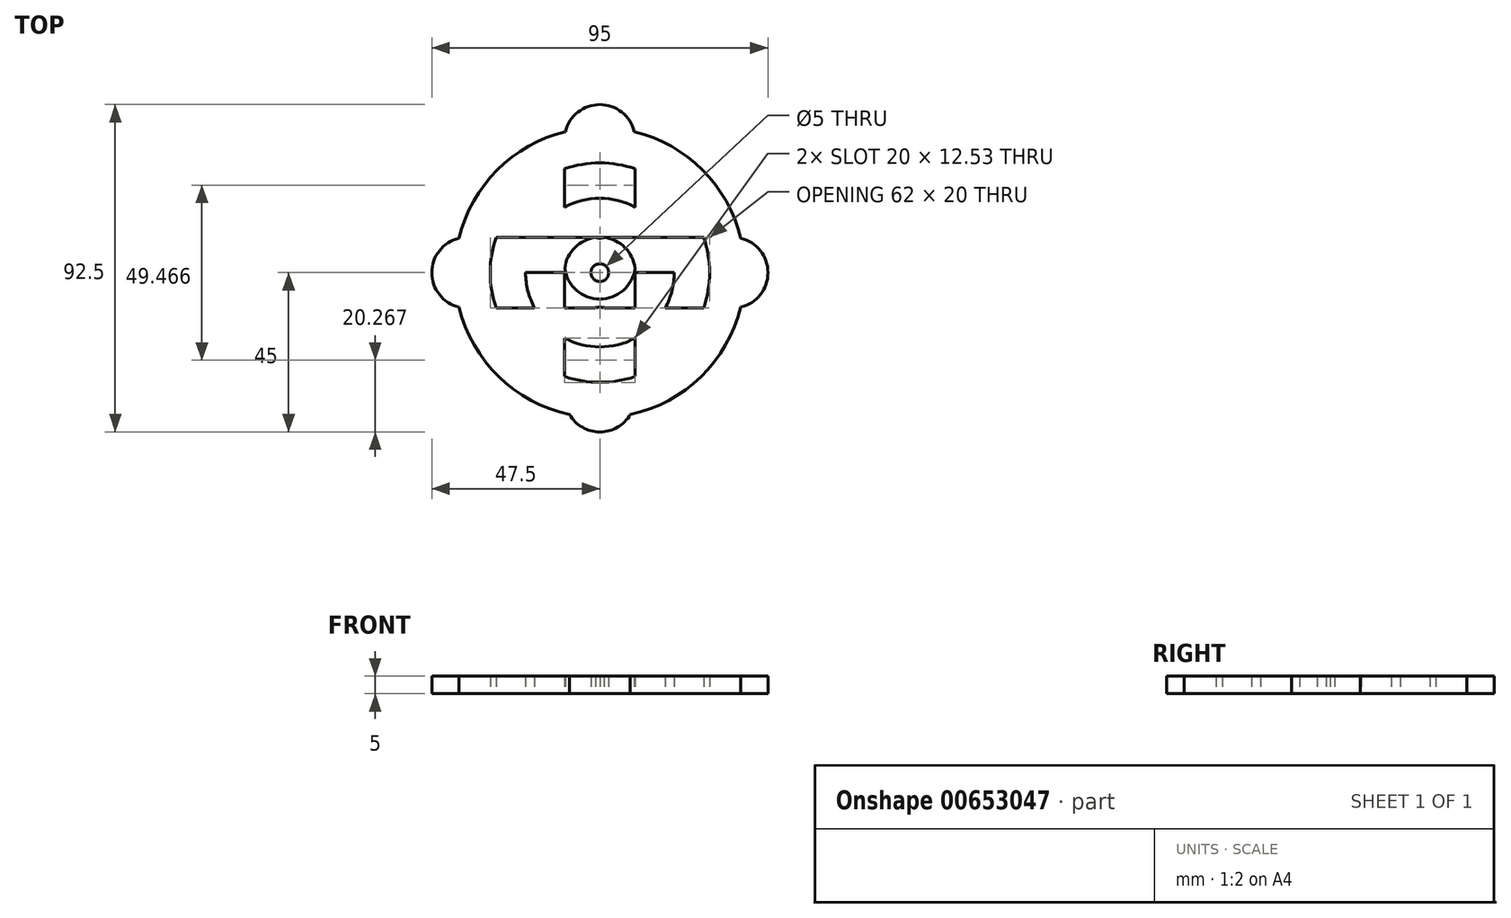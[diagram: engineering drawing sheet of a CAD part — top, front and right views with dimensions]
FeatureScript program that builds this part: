
annotation { "Feature Type Name" : "Feature", "Feature Type Description" : "" }
export const myFeature = defineFeature(function(context is Context, id is Id, definition is map)
    precondition{}
    {
        {
            var Q0;
            Q0=qCreatedBy(makeId("Top.planeOp"),FACE);
            var sketch = newSketch(context, id + "F0", { "sketchPlane" : qUnion([Q0])});
            skCircle(sketch, "E0", {"center": v(0, 0) * mm, "radius": 2.5 * mm});
            skLineSegment(sketch, "E1", {"start": v(0, 2.5) * mm, "end": v(0, 37.5) * mm});
            skLineSegment(sketch, "E2", {"start": v(-2.5, 0) * mm, "end": v(-37.5, 0) * mm});
            skLineSegment(sketch, "E3", {"start": v(0, 0) * mm, "end": v(0, -35) * mm});
            skLineSegment(sketch, "E4", {"start": v(2.5, 0) * mm, "end": v(37.5, 0) * mm});
            skArc(sketch, "E5.0.startCap", {"start": v(10, 2.5) * mm, "mid": v(0, -7.5) * mm, "end": v(-10, 2.5) * mm});
            skArc(sketch, "E5.0.endCap", {"start": v(-10, 37.5) * mm, "mid": v(0, 47.5) * mm, "end": v(10, 37.5) * mm});
            skLineSegment(sketch, "E5.0.left", {"start": v(-10, 2.5) * mm, "end": v(-10, 37.5) * mm});
            skLineSegment(sketch, "E5.0.right", {"start": v(10, 2.5) * mm, "end": v(10, 37.5) * mm});
            skArc(sketch, "E5.1.startCap", {"start": v(2.5, -10) * mm, "mid": v(-7.5, 0) * mm, "end": v(2.5, 10) * mm});
            skArc(sketch, "E5.1.endCap", {"start": v(37.5, 10) * mm, "mid": v(47.5, 0) * mm, "end": v(37.5, -10) * mm});
            skLineSegment(sketch, "E5.1.left", {"start": v(2.5, 10) * mm, "end": v(37.5, 10) * mm});
            skLineSegment(sketch, "E5.1.right", {"start": v(2.5, -10) * mm, "end": v(37.5, -10) * mm});
            skArc(sketch, "E5.2.startCap", {"start": v(-10, 0) * mm, "mid": v(0, 10) * mm, "end": v(10, 0) * mm});
            skArc(sketch, "E5.2.endCap", {"start": v(10, -35) * mm, "mid": v(0, -45) * mm, "end": v(-10, -35) * mm});
            skLineSegment(sketch, "E5.2.left", {"start": v(10, 0) * mm, "end": v(10, -35) * mm});
            skLineSegment(sketch, "E5.2.right", {"start": v(-10, 0) * mm, "end": v(-10, -35) * mm});
            skArc(sketch, "E5.3.startCap", {"start": v(-2.5, 10) * mm, "mid": v(7.5, 0) * mm, "end": v(-2.5, -10) * mm});
            skArc(sketch, "E5.3.endCap", {"start": v(-37.5, -10) * mm, "mid": v(-47.5, 0) * mm, "end": v(-37.5, 10) * mm});
            skLineSegment(sketch, "E5.3.left", {"start": v(-2.5, -10) * mm, "end": v(-37.5, -10) * mm});
            skLineSegment(sketch, "E5.3.right", {"start": v(-2.5, 10) * mm, "end": v(-37.5, 10) * mm});
            skCircle(sketch, "E6", {"center": v(0, 0) * mm, "radius": 21 * mm});
            skCircle(sketch, "E7", {"center": v(0, 0) * mm, "radius": 31 * mm});
            skCircle(sketch, "E8", {"center": v(0, 0) * mm, "radius": 41 * mm});
            skSolve(sketch);
        }
        {
            var Q0;
            Q0 = qSketchRegion(id + "F0", true);
            var Q1;
            {var subQ0=sQuery(id+"F0.wireOp",EDGE,"E6");var subQ1=sQuery(id+"F0.wireOp",EDGE,"E5.1.right");var subQ2=makeQuery(id+"F0.imprint","INTERSECT",VERTEX,{"derivedFrom":[subQ1,subQ0]});Q1=makeQuery(id+"F0.imprint","IMPRINT",FACE,{"disambiguationData":[TD([[makeQuery(id+"F0.imprint","IMPRINT",EDGE,{"disambiguationData":[TD([[subQ2,-1.0]])],"derivedFrom":subQ1}),-1.0]])]});}
            var Q2;
            {var subQ0=sQuery(id+"F0.wireOp",EDGE,"E6");var subQ1=sQuery(id+"F0.wireOp",EDGE,"E5.0.right");var subQ2=makeQuery(id+"F0.imprint","INTERSECT",VERTEX,{"derivedFrom":[subQ1,subQ0]});Q2=makeQuery(id+"F0.imprint","IMPRINT",FACE,{"disambiguationData":[TD([[makeQuery(id+"F0.imprint","IMPRINT",EDGE,{"disambiguationData":[TD([[subQ2,-1.0]])],"derivedFrom":subQ1}),-1.0]])]});}
            var Q3;
            {var subQ0=sQuery(id+"F0.wireOp",EDGE,"E6");var subQ1=sQuery(id+"F0.wireOp",EDGE,"E5.0.left");var subQ2=makeQuery(id+"F0.imprint","INTERSECT",VERTEX,{"derivedFrom":[subQ1,subQ0]});Q3=makeQuery(id+"F0.imprint","IMPRINT",FACE,{"disambiguationData":[TD([[makeQuery(id+"F0.imprint","IMPRINT",EDGE,{"disambiguationData":[TD([[subQ2,-1.0]])],"derivedFrom":subQ1}),1.0]])]});}
            var Q4;
            {var subQ0=sQuery(id+"F0.wireOp",EDGE,"E6");var subQ1=sQuery(id+"F0.wireOp",EDGE,"E5.2.right");var subQ2=makeQuery(id+"F0.imprint","INTERSECT",VERTEX,{"derivedFrom":[subQ1,subQ0]});Q4=makeQuery(id+"F0.imprint","IMPRINT",FACE,{"disambiguationData":[TD([[makeQuery(id+"F0.imprint","IMPRINT",EDGE,{"disambiguationData":[TD([[subQ2,-1.0]])],"derivedFrom":subQ1}),-1.0]])]});}
            var Q5;
            {var subQ0=sQuery(id+"F0.wireOp",EDGE,"E5.2.left");var subQ1=sQuery(id+"F0.wireOp",EDGE,"E5.1.right");var subQ2=makeQuery(id+"F0.imprint","INTERSECT",VERTEX,{"derivedFrom":[subQ1,subQ0]});Q5=makeQuery(id+"F0.imprint","IMPRINT",FACE,{"disambiguationData":[TD([[makeQuery(id+"F0.imprint","IMPRINT",EDGE,{"disambiguationData":[TD([[subQ2,-1.0]])],"derivedFrom":subQ1}),-1.0]])]});}
            var Q6;
            {var subQ0=sQuery(id+"F0.wireOp",EDGE,"E5.3.left");var subQ1=sQuery(id+"F0.wireOp",EDGE,"E5.2.right");var subQ2=makeQuery(id+"F0.imprint","INTERSECT",VERTEX,{"derivedFrom":[subQ1,subQ0]});Q6=makeQuery(id+"F0.imprint","IMPRINT",FACE,{"disambiguationData":[TD([[makeQuery(id+"F0.imprint","IMPRINT",EDGE,{"disambiguationData":[TD([[subQ2,-1.0]])],"derivedFrom":subQ1}),-1.0]])]});}
            var Q7;
            {var subQ0=sQuery(id+"F0.wireOp",EDGE,"E5.3.left");var subQ3=sQuery(id+"F0.wireOp",EDGE,"E5.2.right");var subQ4=makeQuery(id+"F0.imprint","INTERSECT",VERTEX,{"derivedFrom":[subQ3,subQ0]});Q7=makeQuery(id+"F0.imprint","IMPRINT",FACE,{"disambiguationData":[TD([[makeQuery(id+"F0.imprint","IMPRINT",EDGE,{"disambiguationData":[TD([[subQ4,-1.0]])],"derivedFrom":subQ3}),1.0]])]});}
            var Q8;
            {var subQ1=sQuery(id+"F0.wireOp",EDGE,"E5.1.right");var subQ7=sQuery(id+"F0.wireOp",EDGE,"E5.1.startCap");var subQ8=makeQuery(id+"F0.imprint","INTERSECT",VERTEX,{"derivedFrom":[subQ7,subQ1]});Q8=makeQuery(id+"F0.imprint","IMPRINT",FACE,{"disambiguationData":[TD([[makeQuery(id+"F0.imprint","IMPRINT",EDGE,{"disambiguationData":[TD([[subQ8,-1.0]])],"derivedFrom":subQ1}),-1.0]])]});}
            var Q9;
            {var subQ0=sQuery(id+"F0.wireOp",EDGE,"E5.1.left");var subQ1=sQuery(id+"F0.wireOp",EDGE,"E5.0.right");var subQ2=makeQuery(id+"F0.imprint","INTERSECT",VERTEX,{"derivedFrom":[subQ1,subQ0]});Q9=makeQuery(id+"F0.imprint","IMPRINT",FACE,{"disambiguationData":[TD([[makeQuery(id+"F0.imprint","IMPRINT",EDGE,{"disambiguationData":[TD([[subQ2,-1.0]])],"derivedFrom":subQ1}),-1.0]])]});}
            var Q10;
            {var subQ1=sQuery(id+"F0.wireOp",EDGE,"E5.0.right");var subQ5=sQuery(id+"F0.wireOp",EDGE,"E5.0.startCap");var subQ6=makeQuery(id+"F0.imprint","INTERSECT",VERTEX,{"derivedFrom":[subQ5,subQ1]});Q10=makeQuery(id+"F0.imprint","IMPRINT",FACE,{"disambiguationData":[TD([[makeQuery(id+"F0.imprint","IMPRINT",EDGE,{"disambiguationData":[TD([[subQ6,-1.0]])],"derivedFrom":subQ5}),1.0]])]});}
            var Q11;
            {var subQ0=sQuery(id+"F0.wireOp",EDGE,"E5.2.left");var subQ5=sQuery(id+"F0.wireOp",EDGE,"E5.1.right");var subQ6=makeQuery(id+"F0.imprint","INTERSECT",VERTEX,{"derivedFrom":[subQ5,subQ0]});Q11=makeQuery(id+"F0.imprint","IMPRINT",FACE,{"disambiguationData":[TD([[makeQuery(id+"F0.imprint","IMPRINT",EDGE,{"disambiguationData":[TD([[subQ6,-1.0]])],"derivedFrom":subQ5}),1.0]])]});}
            var Q12;
            {var subQ0=sQuery(id+"F0.wireOp",EDGE,"E5.3.right");var subQ1=sQuery(id+"F0.wireOp",EDGE,"E5.0.left");var subQ2=makeQuery(id+"F0.imprint","INTERSECT",VERTEX,{"derivedFrom":[subQ1,subQ0]});Q12=makeQuery(id+"F0.imprint","IMPRINT",FACE,{"disambiguationData":[TD([[makeQuery(id+"F0.imprint","IMPRINT",EDGE,{"disambiguationData":[TD([[subQ2,-1.0]])],"derivedFrom":subQ1}),1.0]])]});}
            var Q13;
            {var subQ3=sQuery(id+"F0.wireOp",EDGE,"E5.2.startCap");var subQ5=sQuery(id+"F0.wireOp",EDGE,"E1");var subQ6=makeQuery(id+"F0.imprint","INTERSECT",VERTEX,{"derivedFrom":[subQ5,subQ3]});Q13=makeQuery(id+"F0.imprint","IMPRINT",FACE,{"disambiguationData":[TD([[makeQuery(id+"F0.imprint","IMPRINT",EDGE,{"disambiguationData":[TD([[subQ6,-1.0]])],"derivedFrom":subQ5}),1.0]])]});}
            var Q14;
            {var subQ5=sQuery(id+"F0.wireOp",EDGE,"E5.2.startCap");var subQ6=sQuery(id+"F0.wireOp",EDGE,"E1");var subQ7=makeQuery(id+"F0.imprint","INTERSECT",VERTEX,{"derivedFrom":[subQ6,subQ5]});Q14=makeQuery(id+"F0.imprint","IMPRINT",FACE,{"disambiguationData":[TD([[makeQuery(id+"F0.imprint","IMPRINT",EDGE,{"disambiguationData":[TD([[subQ7,-1.0]])],"derivedFrom":subQ6}),-1.0]])]});}
            var Q15;
            {var subQ3=sQuery(id+"F0.wireOp",EDGE,"E5.0.startCap");var subQ5=sQuery(id+"F0.wireOp",EDGE,"E5.0.left");var subQ6=makeQuery(id+"F0.imprint","INTERSECT",VERTEX,{"derivedFrom":[subQ3,subQ5]});Q15=makeQuery(id+"F0.imprint","IMPRINT",FACE,{"disambiguationData":[TD([[makeQuery(id+"F0.imprint","IMPRINT",EDGE,{"disambiguationData":[TD([[subQ6,1.0]])],"derivedFrom":subQ3}),1.0]])]});}
            var Q16;
            {var subQ0=sQuery(id+"F0.wireOp",EDGE,"E5.2.right");var subQ5=sQuery(id+"F0.wireOp",EDGE,"E5.3.left");var subQ6=makeQuery(id+"F0.imprint","INTERSECT",VERTEX,{"derivedFrom":[subQ0,subQ5]});Q16=makeQuery(id+"F0.imprint","IMPRINT",FACE,{"disambiguationData":[TD([[makeQuery(id+"F0.imprint","IMPRINT",EDGE,{"disambiguationData":[TD([[subQ6,-1.0]])],"derivedFrom":subQ5}),-1.0]])]});}
            var Q17;
            {var subQ1=sQuery(id+"F0.wireOp",EDGE,"E2");var subQ7=sQuery(id+"F0.wireOp",EDGE,"E5.1.startCap");var subQ8=makeQuery(id+"F0.imprint","INTERSECT",VERTEX,{"derivedFrom":[subQ1,subQ7]});Q17=makeQuery(id+"F0.imprint","IMPRINT",FACE,{"disambiguationData":[TD([[makeQuery(id+"F0.imprint","IMPRINT",EDGE,{"disambiguationData":[TD([[subQ8,-1.0]])],"derivedFrom":subQ1}),-1.0]])]});}
            var Q18;
            {var subQ5=sQuery(id+"F0.wireOp",EDGE,"E5.3.startCap");var subQ6=sQuery(id+"F0.wireOp",EDGE,"E4");var subQ7=makeQuery(id+"F0.imprint","INTERSECT",VERTEX,{"derivedFrom":[subQ6,subQ5]});Q18=makeQuery(id+"F0.imprint","IMPRINT",FACE,{"disambiguationData":[TD([[makeQuery(id+"F0.imprint","IMPRINT",EDGE,{"disambiguationData":[TD([[subQ7,-1.0]])],"derivedFrom":subQ6}),1.0]])]});}
            var Q19;
            {var subQ0=sQuery(id+"F0.wireOp",EDGE,"E5.3.startCap");var subQ1=sQuery(id+"F0.wireOp",EDGE,"E4");var subQ2=makeQuery(id+"F0.imprint","INTERSECT",VERTEX,{"derivedFrom":[subQ1,subQ0]});Q19=makeQuery(id+"F0.imprint","IMPRINT",FACE,{"disambiguationData":[TD([[makeQuery(id+"F0.imprint","IMPRINT",EDGE,{"disambiguationData":[TD([[subQ2,-1.0]])],"derivedFrom":subQ1}),-1.0]])]});}
            var Q20;
            {var subQ5=sQuery(id+"F0.wireOp",EDGE,"E4");var subQ6=sQuery(id+"F0.wireOp",EDGE,"E0");var subQ7=makeQuery(id+"F0.imprint","INTERSECT",VERTEX,{"derivedFrom":[subQ6,subQ5]});Q20=makeQuery(id+"F0.imprint","IMPRINT",FACE,{"disambiguationData":[TD([[makeQuery(id+"F0.imprint","IMPRINT",EDGE,{"disambiguationData":[TD([[subQ7,1.0]])],"derivedFrom":subQ6}),-1.0]])]});}
            var Q21;
            {var subQ5=sQuery(id+"F0.wireOp",EDGE,"E0");var subQ7=sQuery(id+"F0.wireOp",EDGE,"E2");var subQ8=makeQuery(id+"F0.imprint","INTERSECT",VERTEX,{"derivedFrom":[subQ5,subQ7]});Q21=makeQuery(id+"F0.imprint","IMPRINT",FACE,{"disambiguationData":[TD([[makeQuery(id+"F0.imprint","IMPRINT",EDGE,{"disambiguationData":[TD([[subQ8,-1.0]])],"derivedFrom":subQ5}),-1.0]])]});}
            var Q22;
            {var subQ0=sQuery(id+"F0.wireOp",EDGE,"E5.1.startCap");var subQ1=sQuery(id+"F0.wireOp",EDGE,"E2");var subQ2=makeQuery(id+"F0.imprint","INTERSECT",VERTEX,{"derivedFrom":[subQ1,subQ0]});Q22=makeQuery(id+"F0.imprint","IMPRINT",FACE,{"disambiguationData":[TD([[makeQuery(id+"F0.imprint","IMPRINT",EDGE,{"disambiguationData":[TD([[subQ2,-1.0]])],"derivedFrom":subQ1}),1.0]])]});}
            var Q23;
            {var subQ0=sQuery(id+"F0.wireOp",EDGE,"E5.0.startCap");var subQ1=sQuery(id+"F0.wireOp",EDGE,"E3");var subQ2=makeQuery(id+"F0.imprint","INTERSECT",VERTEX,{"derivedFrom":[subQ1,subQ0]});Q23=makeQuery(id+"F0.imprint","IMPRINT",FACE,{"disambiguationData":[TD([[makeQuery(id+"F0.imprint","IMPRINT",EDGE,{"disambiguationData":[TD([[subQ2,-1.0]])],"derivedFrom":subQ0}),1.0]])]});}
            var Q24;
            {var subQ0=sQuery(id+"F0.wireOp",EDGE,"E5.0.startCap");var subQ1=sQuery(id+"F0.wireOp",EDGE,"E3");var subQ2=makeQuery(id+"F0.imprint","INTERSECT",VERTEX,{"derivedFrom":[subQ1,subQ0]});Q24=makeQuery(id+"F0.imprint","IMPRINT",FACE,{"disambiguationData":[TD([[makeQuery(id+"F0.imprint","IMPRINT",EDGE,{"disambiguationData":[TD([[subQ2,1.0]])],"derivedFrom":subQ0}),1.0]])]});}
            var Q25;
            {var subQ0=sQuery(id+"F0.wireOp",EDGE,"E1");var subQ1=sQuery(id+"F0.wireOp",EDGE,"E0");var subQ2=makeQuery(id+"F0.imprint","INTERSECT",VERTEX,{"derivedFrom":[subQ1,subQ0]});Q25=makeQuery(id+"F0.imprint","IMPRINT",FACE,{"disambiguationData":[TD([[makeQuery(id+"F0.imprint","IMPRINT",EDGE,{"disambiguationData":[TD([[subQ2,1.0]])],"derivedFrom":subQ1}),-1.0]])]});}
            var Q26;
            {var subQ0=sQuery(id+"F0.wireOp",EDGE,"E1");var subQ1=sQuery(id+"F0.wireOp",EDGE,"E0");var subQ2=makeQuery(id+"F0.imprint","INTERSECT",VERTEX,{"derivedFrom":[subQ1,subQ0]});Q26=makeQuery(id+"F0.imprint","IMPRINT",FACE,{"disambiguationData":[TD([[makeQuery(id+"F0.imprint","IMPRINT",EDGE,{"disambiguationData":[TD([[subQ2,-1.0]])],"derivedFrom":subQ1}),-1.0]])]});}
            extrude(context, id + "F1", {"entities" : qUnion([Q0, Q1, Q2, Q3, Q4, Q5, Q6, Q7, Q8, Q9, Q10, Q11, Q12, Q13, Q14, Q15, Q16, Q17, Q18, Q19, Q20, Q21, Q22, Q23, Q24, Q25, Q26]), "depth" : 5 * mm, "offsetDistance" : 25 * mm});
        }
    });
